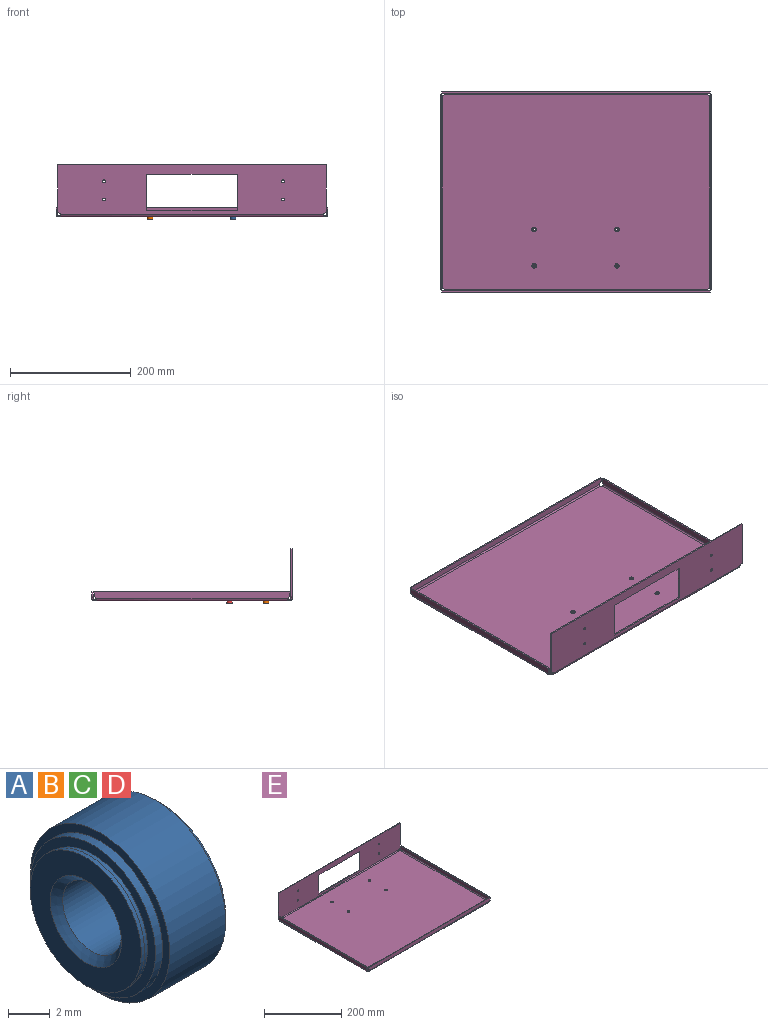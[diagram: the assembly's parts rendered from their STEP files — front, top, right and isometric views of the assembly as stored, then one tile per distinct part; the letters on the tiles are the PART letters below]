
ASSEMBLY  parts=5 mates=1
PART A: 51 faces, bbox 5x9.4x9.4 mm
  f0: cylinder r=3.75mm len=7.49mm, axis (1,0,0), area 5.2mm2, adj f2,f3
  f1: plane 0.31x0.21mm, normal (1,0,0), area 0.1mm2, adj f4,f5,f6,f7
  f2: plane 7.49x7.49mm, normal (-1,0,0), area 25.8mm2, adj f0,f8
  f3: cone r=3.66mm half-angle=13.5deg, axis (-1,0,0), area 6.2mm2, adj f0,f9
  f4: cylinder r=0.11mm len=0.21mm, axis (-1,0,0), area 0mm2, adj f1,f5,f7,f10
  f5: plane 0.2x0.03mm, normal (0,0,1), area 0mm2, adj f1,f4,f6,f10
  f6: plane 0.21x0.03mm, normal (0,-1,0), area 0mm2, adj f1,f5,f7,f10
  f7: plane 0.2x0.03mm, normal (0,0,-1), area 0mm2, adj f1,f4,f6,f10
  f8: cone r=2.2mm half-angle=45deg, axis (-1,0,0), area 8.4mm2, adj f2,f13
  f9: plane 8.45x8.45mm, normal (-1,0,0), area 13.4mm2, adj f3,f14
  f10: plane 0.82x0.7mm, normal (1,0,0), area 0.3mm2, adj f4,f5,f6,f7,f15,f16,f17,f18
  f11: plane 1.22x1.18mm, normal (1,0,0), area 0.5mm2, adj f21,f22,f23,f24,f25,f26,f27,f28
  f12: plane 1.04x0.97mm, normal (1,0,0), area 0.4mm2, adj f34,f35,f36,f37,f38,f39,f40,f41
  f13: cylinder r=1.98mm len=4.17mm, axis (-1,0,0), area 52mm2, adj f8,f46
  f14: cylinder r=4.22mm len=8.45mm, axis (-1,0,0), area 12.8mm2, adj f9,f47
  f15: plane 0.25x0.03mm, normal (0,0,1), area 0mm2, adj f10,f16,f20,f49
  f16: cylinder r=0.26mm len=0.51mm, axis (-1,0,0), area 0mm2, adj f10,f15,f17,f49
  f17: plane 0.44x0.03mm, normal (0,0,-1), area 0mm2, adj f10,f16,f18,f49
  f18: plane 0.82x0.03mm, normal (0,1,0), area 0mm2, adj f10,f17,f19,f49
  f19: plane 0.19x0.03mm, normal (0,0,1), area 0mm2, adj f10,f18,f20,f49
  f20: plane 0.31x0.03mm, normal (0,-1,0), area 0mm2, adj f10,f15,f19,f49
  f21: plane 0.69x0.17mm, normal (0,0.24,-0.97), area 0mm2, adj f11,f22,f33,f49
  f22: plane 0.59x0.34mm, normal (0,-0.5,0.87), area 0mm2, adj f11,f21,f23,f49
  f23: plane 0.17x0.1mm, normal (0,-0.87,-0.5), area 0mm2, adj f11,f22,f24,f49
  f24: plane 0.71x0.41mm, normal (0,0.5,-0.87), area 0mm2, adj f11,f23,f25,f49
  f25: plane 0.28x0.16mm, normal (0,0.87,0.5), area 0mm2, adj f11,f24,f26,f49
  f26: plane 0.56x0.16mm, normal (0,-0.27,0.96), area 0mm2, adj f11,f25,f27,f49
  f27: plane 0.42x0.41mm, normal (0,0.7,-0.72), area 0mm2, adj f11,f26,f28,f49
  f28: plane 0.28x0.16mm, normal (0,0.87,0.5), area 0mm2, adj f11,f27,f29,f49
  f29: plane 0.71x0.41mm, normal (0,-0.5,0.87), area 0mm2, adj f11,f28,f30,f49
  f30: plane 0.17x0.1mm, normal (0,-0.87,-0.5), area 0mm2, adj f11,f29,f31,f49
  f31: plane 0.59x0.34mm, normal (0,0.5,-0.87), area 0mm2, adj f11,f30,f32,f49
  f32: plane 0.51x0.49mm, normal (0,-0.72,0.69), area 0mm2, adj f11,f31,f33,f49
  f33: plane 0.13x0.08mm, normal (0,-0.87,-0.5), area 0mm2, adj f11,f21,f32,f49
  f34: plane 0.36x0.21mm, normal (0,0.87,-0.5), area 0mm2, adj f12,f35,f45,f49
  f35: plane 0.13x0.08mm, normal (0,0.5,0.87), area 0mm2, adj f12,f34,f36,f49
  f36: plane 0.36x0.21mm, normal (0,-0.87,0.5), area 0mm2, adj f12,f35,f37,f49
  f37: plane 0.16x0.09mm, normal (0,0.5,0.87), area 0mm2, adj f12,f36,f38,f49
  f38: plane 0.39x0.22mm, normal (0,0.87,-0.5), area 0mm2, adj f12,f37,f39,f49
  f39: plane 0.13x0.07mm, normal (0,0.5,0.87), area 0mm2, adj f12,f38,f40,f49
  f40: plane 0.56x0.33mm, normal (0,-0.87,0.5), area 0mm2, adj f12,f39,f41,f49
  f41: plane 0.71x0.41mm, normal (0,-0.5,-0.87), area 0mm2, adj f12,f40,f42,f49
  f42: plane 0.56x0.33mm, normal (0,0.87,-0.5), area 0mm2, adj f12,f41,f43,f49
  f43: plane 0.13x0.07mm, normal (0,0.5,0.87), area 0mm2, adj f12,f42,f44,f49
  f44: plane 0.39x0.22mm, normal (0,-0.87,0.5), area 0mm2, adj f12,f43,f45,f49
  f45: plane 0.16x0.09mm, normal (0,0.5,0.87), area 0mm2, adj f12,f34,f44,f49
  f46: cone r=2.2mm half-angle=45deg, axis (1,0,0), area 8.4mm2, adj f13,f49
  f47: plane 9.4x9.4mm, normal (-1,0,0), area 13.3mm2, adj f14,f48
  f48: cylinder r=4.7mm len=9.4mm, axis (1,0,0), area 111.7mm2, adj f47,f50
  f49: plane 8.83x8.83mm, normal (1,0,0), area 41.7mm2, adj f15,f16,f17,f18,f19,f20,f21,f22
  f50: cone r=4.56mm half-angle=45deg, axis (-1,0,0), area 11.4mm2, adj f48,f49
PART B: same geometry as A
PART C: same geometry as A
PART D: same geometry as A
PART E: 62 faces, bbox 449.1x331.6x86.5 mm
  f0: plane 439.93x322.45mm, normal (0,0,-1), area 141666.1mm2, adj f1,f2,f3,f4,f6,f7,f8,f9
  f1: cylinder r=3.76mm len=7.52mm, axis (0,0,-1), area 54mm2, adj f0,f5
  f2: cylinder r=3.76mm len=7.52mm, axis (0,0,-1), area 54mm2, adj f0,f5
  f3: cylinder r=3.76mm len=7.52mm, axis (0,0,-1), area 54mm2, adj f0,f5
  f4: cylinder r=3.76mm len=7.52mm, axis (0,0,-1), area 54mm2, adj f0,f5
  f5: plane 439.93x322.45mm, normal (0,0,1), area 141666.1mm2, adj f1,f2,f3,f4,f6,f7,f8,f9
  f6: cylinder r=5.52mm len=2.29mm, axis (0,0,1), area 7.4mm2, adj f0,f5,f18,f48
  f7: cylinder r=5.52mm len=2.29mm, axis (0,0,1), area 7.4mm2, adj f0,f5,f37,f47
  f8: cylinder r=5.52mm len=2.29mm, axis (0,0,1), area 7.4mm2, adj f0,f5,f36,f59
  f9: cylinder r=5.52mm len=2.29mm, axis (0,0,1), area 7.4mm2, adj f0,f5,f17,f58
  f10: plane 7.53x2.29mm, normal (-1,0,0), area 17.2mm2, adj f12,f13,f14,f15
  f11: plane 7.53x2.29mm, normal (1,0,0), area 17.2mm2, adj f12,f13,f14,f16
  f12: plane 444.5x10.44mm, normal (0,-1,0), area 4621.9mm2, adj f10,f11,f13,f15,f16,f19
  f13: plane 444.5x2.29mm, normal (0,0,1), area 1016.1mm2, adj f10,f11,f12,f14
  f14: plane 444.5x10.44mm, normal (0,1,0), area 4621.9mm2, adj f10,f11,f13,f15,f16,f20
  f15: cylinder r=5.52mm len=4.55mm, axis (0,1,0), area 12.9mm2, adj f10,f12,f14,f18
  f16: cylinder r=5.52mm len=4.55mm, axis (0,1,0), area 12.9mm2, adj f11,f12,f14,f17
  f17: bspline ~4.57x4.57mm, area 12.8mm2, adj f9,f16,f19,f20
  f18: bspline ~4.57x4.57mm, area 12.8mm2, adj f6,f15,f19,f20
  f19: cylinder r=4.57mm len=435.39mm, axis (1,0,0), area 3120.5mm2, adj f0,f12,f17,f18
  f20: cylinder r=2.29mm len=435.39mm, axis (1,0,0), area 1560.3mm2, adj f5,f14,f17,f18
  f21: plane 78.98x2.29mm, normal (1,0,0), area 180.5mm2, adj f23,f27,f33,f34
  f22: plane 78.98x2.29mm, normal (-1,0,0), area 180.5mm2, adj f23,f27,f33,f35
  f23: plane 444.5x81.89mm, normal (0,1,0), area 27309.7mm2, adj f21,f22,f24,f25,f26,f27,f28,f29
  f24: plane 150x2.29mm, normal (0,0,1), area 342.9mm2, adj f23,f25,f32,f33
  f25: plane 60x2.29mm, normal (-1,0,0), area 137.2mm2, adj f23,f24,f26,f33
  f26: plane 150x2.29mm, normal (0,0,-1), area 342.9mm2, adj f23,f25,f32,f33
  f27: plane 444.5x2.29mm, normal (0,0,1), area 1016.1mm2, adj f21,f22,f23,f33
  f28: cylinder r=2.39mm len=4.78mm, axis (0,1,0), area 34.3mm2, adj f23,f33
  f29: cylinder r=2.39mm len=4.78mm, axis (0,1,0), area 34.3mm2, adj f23,f33
  f30: cylinder r=2.39mm len=4.78mm, axis (0,1,0), area 34.3mm2, adj f23,f33
  f31: cylinder r=2.39mm len=4.78mm, axis (0,1,0), area 34.3mm2, adj f23,f33
  f32: plane 60x2.29mm, normal (1,0,0), area 137.2mm2, adj f23,f24,f26,f33
  f33: plane 444.5x81.89mm, normal (0,-1,0), area 27309.7mm2, adj f21,f22,f24,f25,f26,f27,f28,f29
  f34: cylinder r=5.52mm len=4.55mm, axis (0,-1,0), area 12.9mm2, adj f21,f23,f33,f36
  f35: cylinder r=5.52mm len=4.55mm, axis (0,-1,0), area 12.9mm2, adj f22,f23,f33,f37
  f36: bspline ~4.57x4.57mm, area 12.8mm2, adj f8,f34,f38,f39
  f37: bspline ~4.57x4.57mm, area 12.8mm2, adj f7,f35,f38,f39
  f38: cylinder r=4.57mm len=435.39mm, axis (1,0,0), area 3120.5mm2, adj f0,f23,f36,f37
  f39: cylinder r=2.29mm len=435.39mm, axis (1,0,0), area 1560.3mm2, adj f5,f33,f36,f37
  f40: plane 8.17x2.29mm, normal (0,1,0), area 18.7mm2, adj f42,f43,f44,f45
  f41: plane 8.17x2.29mm, normal (0,-1,0), area 18.7mm2, adj f42,f43,f44,f46
  f42: plane 322.45x10.44mm, normal (-1,0,0), area 3360.1mm2, adj f40,f41,f43,f45,f46,f49
  f43: plane 322.45x2.29mm, normal (0,0,1), area 737.1mm2, adj f40,f41,f42,f44
  f44: plane 322.45x10.44mm, normal (1,0,0), area 3360.1mm2, adj f40,f41,f43,f45,f46,f50
  f45: cylinder r=5.52mm len=2.29mm, axis (1,0,0), area 7.4mm2, adj f40,f42,f44,f47
  f46: cylinder r=5.52mm len=2.29mm, axis (1,0,0), area 7.4mm2, adj f41,f42,f44,f48
  f47: bspline ~4.57x4.57mm, area 12.8mm2, adj f7,f45,f49,f50
  f48: bspline ~4.57x4.57mm, area 12.8mm2, adj f6,f46,f49,f50
  f49: cylinder r=4.57mm len=317.92mm, axis (0,1,0), area 2276.9mm2, adj f0,f42,f47,f48
  f50: cylinder r=2.29mm len=317.92mm, axis (0,1,0), area 1138.4mm2, adj f5,f44,f47,f48
  f51: plane 8.17x2.29mm, normal (0,-1,0), area 18.7mm2, adj f53,f54,f55,f56
  f52: plane 8.17x2.29mm, normal (0,1,0), area 18.7mm2, adj f53,f54,f55,f57
  f53: plane 322.45x10.44mm, normal (1,0,0), area 3360.1mm2, adj f51,f52,f54,f56,f57,f60
  f54: plane 322.45x2.29mm, normal (0,0,1), area 737.1mm2, adj f51,f52,f53,f55
  f55: plane 322.45x10.44mm, normal (-1,0,0), area 3360.1mm2, adj f51,f52,f54,f56,f57,f61
  f56: cylinder r=5.52mm len=2.29mm, axis (-1,0,0), area 7.4mm2, adj f51,f53,f55,f58
  f57: cylinder r=5.52mm len=2.29mm, axis (-1,0,0), area 7.4mm2, adj f52,f53,f55,f59
  f58: bspline ~4.57x4.57mm, area 12.8mm2, adj f9,f56,f60,f61
  f59: bspline ~4.57x4.57mm, area 12.8mm2, adj f8,f57,f60,f61
  f60: cylinder r=4.57mm len=317.92mm, axis (0,-1,0), area 2276.9mm2, adj f0,f53,f58,f59
  f61: cylinder r=2.29mm len=317.92mm, axis (0,-1,0), area 1138.4mm2, adj f5,f55,f58,f59
PLACE A rot(axis=(0.71,0,-0.71),180deg) t=(-165.65,64.34,-17.78)mm
PLACE B rot(axis=(0.71,0,-0.71),180deg) t=(-302.65,64.34,-17.78)mm
PLACE C rot(axis=(0.71,0,-0.71),180deg) t=(-165.65,124.34,-17.78)mm
PLACE D rot(axis=(0.71,0,-0.71),180deg) t=(-302.65,124.34,-17.78)mm
PLACE E rot(axis=(0,0,1),180deg) t=(-227.56,186.56,-16.46)mm fixed
MATE fastened E.f4 <-> A.f14  axis (0,0,-1) through (-165.65,64.34,-18.74)mm
